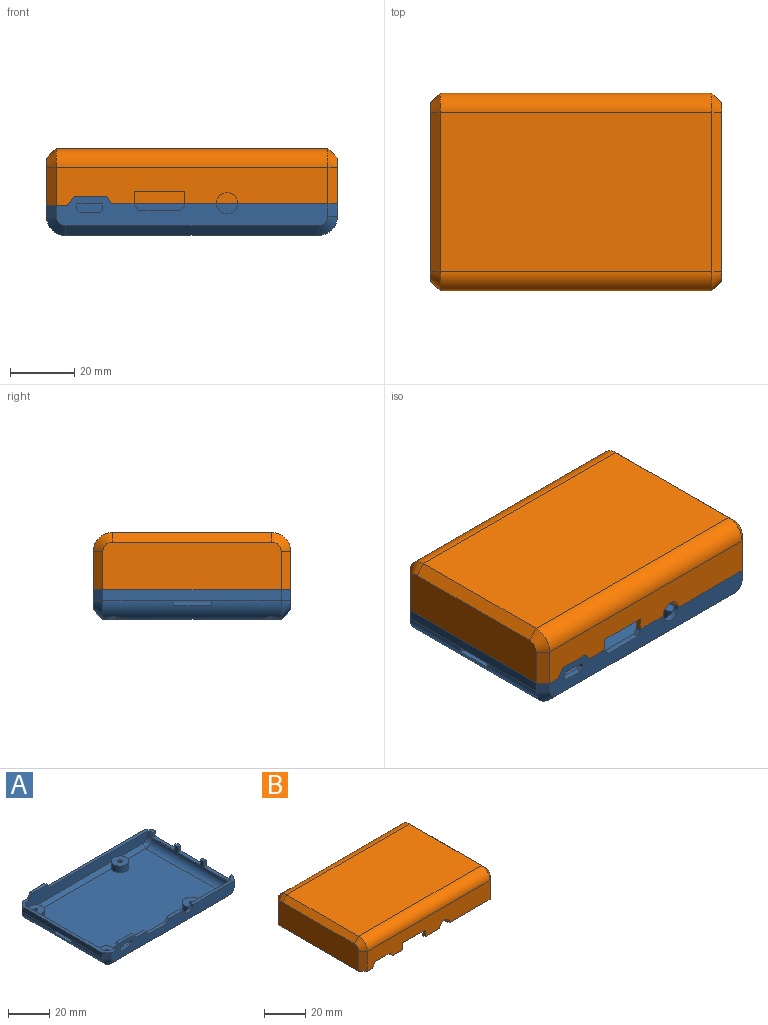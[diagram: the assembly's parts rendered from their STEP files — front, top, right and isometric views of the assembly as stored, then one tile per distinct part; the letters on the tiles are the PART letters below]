
ASSEMBLY  parts=2 mates=1
PART A: 98 faces, bbox 90.4x61.4x12.2 mm
  f0: plane 82.91x8.44mm, normal (0,1,0), area 457.5mm2, adj f8,f9,f10,f12,f14,f59,f60,f61
  f1: plane 84.4x9.18mm, normal (0,-1,0), area 527.3mm2, adj f41,f42,f43,f45,f47,f59,f60,f61
  f2: plane 53.91x3.8mm, normal (-1,0,0), area 48.1mm2, adj f6,f8,f11,f26,f27,f28,f29,f30
  f3: plane 78.4x53.91mm, normal (0,0,1), area 4076.9mm2, adj f6,f7,f10,f15,f18,f20,f22,f24
  f4: plane 53.91x3.18mm, normal (1,0,0), area 171.2mm2, adj f7,f14,f17,f72,f88
  f5: plane 82.91x8.44mm, normal (0,-1,0), area 525.6mm2, adj f11,f13,f15,f16,f17,f87,f88,f89
  f6: cylinder r=4.2mm len=53.91mm, axis (0,1,0), area 355.7mm2, adj f2,f3,f9,f13
  f7: cylinder r=4.2mm len=53.91mm, axis (0,-1,0), area 275.8mm2, adj f3,f4,f12,f16,f18,f20,f71,f73
  f8: plane 3.8x1.95mm, normal (-0.71,0.71,0), area 10.4mm2, adj f0,f2,f9,f85
  f9: cone r=1.73mm half-angle=45deg, axis (0,1,0), area 13.9mm2, adj f0,f6,f8,f10
  f10: plane 78.4x1.95mm, normal (0,0.71,0.71), area 195.8mm2, adj f0,f3,f9,f12,f18,f24
  f11: plane 3.8x1.95mm, normal (-0.71,-0.71,0), area 10.4mm2, adj f2,f5,f13,f87
  f12: cone r=1.73mm half-angle=45deg, axis (0,1,0), area 7.2mm2, adj f0,f7,f10,f14,f18
  f13: cone r=1.73mm half-angle=45deg, axis (0,-1,0), area 13.9mm2, adj f5,f6,f11,f15
  f14: plane 3.18x1.95mm, normal (0.71,0.71,0), area 8.7mm2, adj f0,f4,f12,f88
  f15: plane 78.4x1.95mm, normal (0,-0.71,0.71), area 195.8mm2, adj f3,f5,f13,f16,f20,f22
  f16: cone r=1.73mm half-angle=45deg, axis (0,-1,0), area 7.2mm2, adj f5,f7,f15,f17,f20
  f17: plane 3.18x1.95mm, normal (0.71,-0.71,0), area 8.7mm2, adj f4,f5,f16,f88
  f18: cylinder r=4.3mm len=8.6mm, axis (0,0,-1), area 76.6mm2, adj f3,f7,f10,f12,f19
  f19: plane 8.6x8.6mm, normal (0,0,1), area 54.9mm2, adj f18,f78
  f20: cylinder r=4.3mm len=8.6mm, axis (0,0,-1), area 76.6mm2, adj f3,f7,f15,f16,f21
  f21: plane 8.6x8.6mm, normal (0,0,1), area 54.9mm2, adj f20,f77
  f22: cylinder r=4.3mm len=8.6mm, axis (0,0,-1), area 95.3mm2, adj f3,f15,f23
  f23: plane 8.6x8.6mm, normal (0,0,1), area 54.9mm2, adj f22,f76
  f24: cylinder r=4.3mm len=8.6mm, axis (0,0,-1), area 95.3mm2, adj f3,f10,f25
  f25: plane 8.6x8.6mm, normal (0,0,1), area 54.9mm2, adj f24,f75
  f26: plane 3.3x1.8mm, normal (0,1,0), area 5.9mm2, adj f2,f27,f35,f97
  f27: plane 15x1.8mm, normal (0,0,1), area 27mm2, adj f2,f26,f28,f35
  f28: plane 3.3x1.8mm, normal (0,-1,0), area 5.9mm2, adj f2,f27,f35,f87
  f29: plane 3.3x1.8mm, normal (0,1,0), area 5.9mm2, adj f2,f30,f35,f96
  f30: plane 15x1.8mm, normal (0,0,1), area 27mm2, adj f2,f29,f31,f35
  f31: plane 3.3x1.8mm, normal (0,-1,0), area 5.9mm2, adj f2,f30,f35,f97
  f32: plane 3.3x1.8mm, normal (0,1,0), area 5.9mm2, adj f2,f33,f35,f85
  f33: plane 17.5x1.8mm, normal (0,0,1), area 31.5mm2, adj f2,f32,f34,f35
  f34: plane 3.3x1.8mm, normal (0,-1,0), area 5.9mm2, adj f2,f33,f35,f96
  f35: plane 55.4x3.8mm, normal (1,0,0), area 53.7mm2, adj f26,f27,f28,f29,f30,f31,f32,f33
  f36: plane 78.4x55.4mm, normal (0,0,-1), area 4256.1mm2, adj f39,f40,f43,f48,f79,f81,f83,f84
  f37: plane 55.4x3.18mm, normal (-1,0,0), area 175.9mm2, adj f40,f47,f50,f72,f88
  f38: plane 84.4x9.18mm, normal (0,1,0), area 595.4mm2, adj f44,f46,f48,f49,f50,f87,f88,f89
  f39: cylinder r=6mm len=55.4mm, axis (0,1,0), area 522.1mm2, adj f35,f36,f42,f46
  f40: cylinder r=6mm len=55.4mm, axis (0,-1,0), area 471.3mm2, adj f36,f37,f45,f49,f71,f73,f74,f80
  f41: plane 3.8x3mm, normal (0.71,-0.71,0), area 16.1mm2, adj f1,f35,f42,f85
  f42: cone r=3mm half-angle=45deg, axis (0,1,0), area 30mm2, adj f1,f39,f41,f43
  f43: plane 78.4x3mm, normal (0,-0.71,-0.71), area 332.6mm2, adj f1,f36,f42,f45
  f44: plane 3.8x3mm, normal (0.71,0.71,0), area 16.1mm2, adj f35,f38,f46,f87
  f45: cone r=3mm half-angle=45deg, axis (0,1,0), area 30mm2, adj f1,f40,f43,f47
  f46: cone r=3mm half-angle=45deg, axis (0,-1,0), area 30mm2, adj f38,f39,f44,f48
  f47: plane 3.18x3mm, normal (-0.71,-0.71,0), area 13.5mm2, adj f1,f37,f45,f88
  f48: plane 78.4x3mm, normal (0,0.71,-0.71), area 332.6mm2, adj f36,f38,f46,f49
  f49: cone r=3mm half-angle=45deg, axis (0,-1,0), area 30mm2, adj f38,f40,f48,f50
  f50: plane 3.18x3mm, normal (-0.71,0.71,0), area 13.5mm2, adj f37,f38,f49,f88
  f51: cylinder r=2.5mm len=5mm, axis (0,0,-1), area 50.6mm2, adj f52,f81,f82
  f52: plane 5x5mm, normal (0,0,-1), area 16.5mm2, adj f51,f78
  f53: cylinder r=2.5mm len=5mm, axis (0,0,-1), area 50.6mm2, adj f54,f79,f80
  f54: plane 5x5mm, normal (0,0,-1), area 16.5mm2, adj f53,f77
  f55: cylinder r=2.5mm len=5mm, axis (0,0,-1), area 53.4mm2, adj f56,f84
  f56: plane 5x5mm, normal (0,0,-1), area 16.5mm2, adj f55,f76
  f57: cylinder r=2.5mm len=5mm, axis (0,0,-1), area 53.4mm2, adj f58,f83
  f58: plane 5x5mm, normal (0,0,-1), area 16.5mm2, adj f57,f75
  f59: plane 1.81x1.8mm, normal (-1,0,0), area 3.3mm2, adj f0,f1,f60,f64
  f60: plane 8x1.8mm, normal (0,0,-1), area 14.4mm2, adj f0,f1,f59,f61
  f61: plane 1.84x1.8mm, normal (1,0,0), area 3.3mm2, adj f0,f1,f60,f62
  f62: plane 1.8x0.99mm, normal (0.71,0,0.71), area 2.5mm2, adj f0,f1,f61,f63
  f63: plane 6x1.8mm, normal (0,0,1), area 10.8mm2, adj f0,f1,f62,f64
  f64: plane 1.8x1.01mm, normal (-0.71,0,0.71), area 2.6mm2, adj f0,f1,f59,f63
  f65: plane 12.79x1.8mm, normal (0,0,1), area 23mm2, adj f0,f1,f66,f69
  f66: plane 1.8x1.45mm, normal (-0.75,0,0.66), area 3.5mm2, adj f0,f1,f65,f67
  f67: plane 1.8x0.67mm, normal (-1,0,0), area 1.2mm2, adj f0,f1,f66,f86
  f68: plane 1.8x0.38mm, normal (1,0,0), area 0.7mm2, adj f0,f1,f69,f94
  f69: plane 1.8x1.74mm, normal (0.75,0,0.66), area 4.2mm2, adj f0,f1,f65,f68
  f70: cylinder r=3.3mm len=6.59mm, axis (0,1,0), area 17.9mm2, adj f0,f1,f85,f86
  f71: plane 2.21x1.8mm, normal (0,-1,0), area 3.3mm2, adj f7,f40,f72,f74
  f72: plane 11.8x1.8mm, normal (0,0,-1), area 21.2mm2, adj f4,f37,f71,f73
  f73: plane 2.21x1.8mm, normal (0,1,0), area 3.3mm2, adj f7,f40,f72,f74
  f74: plane 11.8x1.93mm, normal (0,0,1), area 22.8mm2, adj f7,f40,f71,f73
  f75: cylinder r=1mm len=2mm, axis (0,0,-1), area 11.3mm2, adj f25,f58
  f76: cylinder r=1mm len=2mm, axis (0,0,-1), area 11.3mm2, adj f23,f56
  f77: cylinder r=1mm len=2mm, axis (0,0,-1), area 11.3mm2, adj f21,f54
  f78: cylinder r=1mm len=2mm, axis (0,0,-1), area 11.3mm2, adj f19,f52
  f79: torus R=3mm, axis (0,0,1), area 6.9mm2, adj f36,f53,f80
  f80: bspline ~6.01x3.73mm, area 7.7mm2, adj f40,f53,f79
  f81: torus R=3mm, axis (0,0,1), area 6.9mm2, adj f36,f51,f82
  f82: bspline ~6.01x3.73mm, area 7.7mm2, adj f40,f51,f81
  f83: torus R=3mm, axis (0,0,1), area 13.2mm2, adj f36,f57
  f84: torus R=3mm, axis (0,0,1), area 13.2mm2, adj f36,f55
  f85: plane 31.01x4.55mm, normal (0,0,1), area 58.2mm2, adj f0,f1,f2,f8,f32,f35,f41,f70
  f86: plane 10.01x1.8mm, normal (0,0,1), area 18mm2, adj f0,f1,f67,f70
  f87: plane 70.18x4.35mm, normal (0,0,1), area 128.3mm2, adj f2,f5,f11,f28,f35,f38,f44,f91
  f88: plane 61.4x6.44mm, normal (0,0,1), area 122mm2, adj f0,f1,f4,f5,f14,f17,f37,f38
  f89: plane 3.01x2.17mm, normal (-0.81,0,0.58), area 6.7mm2, adj f5,f38,f88,f90
  f90: plane 10.07x1.8mm, normal (0,0,1), area 18.1mm2, adj f5,f38,f89,f91
  f91: plane 2.39x1.8mm, normal (0.84,0,0.54), area 5.1mm2, adj f5,f38,f87,f90
  f92: plane 3.01x2.17mm, normal (-0.81,0,0.58), area 6.7mm2, adj f0,f1,f88,f93
  f93: plane 10.07x1.8mm, normal (0,0,1), area 18.1mm2, adj f0,f1,f92,f95
  f94: plane 6.98x1.8mm, normal (0,0,1), area 12.6mm2, adj f0,f1,f68,f95
  f95: plane 2.39x1.8mm, normal (0.84,0,0.54), area 5.1mm2, adj f0,f1,f93,f94
  f96: plane 2.4x1.8mm, normal (0,0,1), area 4.3mm2, adj f2,f29,f34,f35
  f97: plane 2.6x1.8mm, normal (0,0,1), area 4.7mm2, adj f2,f26,f31,f35
PART B: 81 faces, bbox 90.4x61.4x20 mm
  f0: cylinder r=4.2mm len=82.91mm, axis (-1,0,0), area 528.6mm2, adj f1,f2,f8,f47,f62,f71
  f1: cone r=1.73mm half-angle=45deg, axis (1,0,0), area 13.9mm2, adj f0,f6,f43,f44,f62
  f2: plane 82.91x49.4mm, normal (0,0,-1), area 4052.5mm2, adj f0,f5,f6,f7,f62,f67,f71,f77
  f3: plane 84.4x49.4mm, normal (0,0,1), area 4169.4mm2, adj f4,f14,f15,f16
  f4: cylinder r=6mm len=84.4mm, axis (-1,0,0), area 795.5mm2, adj f3,f17,f19,f46
  f5: plane 49.4x1.95mm, normal (-0.71,0,-0.71), area 135.9mm2, adj f2,f8,f10,f39
  f6: plane 49.45x1.99mm, normal (0.71,0,-0.71), area 135.9mm2, adj f1,f2,f9,f44,f62,f67
  f7: cylinder r=4.2mm len=82.91mm, axis (1,0,0), area 528.6mm2, adj f2,f9,f10,f42,f67,f77
  f8: cone r=1.73mm half-angle=45deg, axis (-1,0,0), area 13.9mm2, adj f0,f5,f25,f39
  f9: cone r=1.73mm half-angle=45deg, axis (1,0,0), area 13.9mm2, adj f6,f7,f40,f44,f67
  f10: cone r=1.73mm half-angle=45deg, axis (-1,0,0), area 13.8mm2, adj f5,f7,f11,f37,f39,f41,f45
  f11: plane 15x2.14mm, normal (0,0,-1), area 27.1mm2, adj f10,f32,f37,f38,f39
  f12: plane 15x1.8mm, normal (0,0,-1), area 27mm2, adj f32,f35,f36,f39
  f13: plane 17.5x1.8mm, normal (0,0,-1), area 31.5mm2, adj f32,f33,f34,f39
  f14: plane 49.4x3mm, normal (0.71,0,0.71), area 209.6mm2, adj f3,f17,f18,f32
  f15: plane 49.4x3mm, normal (-0.71,0,0.71), area 209.6mm2, adj f3,f19,f20,f31
  f16: cylinder r=6mm len=84.4mm, axis (1,0,0), area 795.5mm2, adj f3,f18,f20,f29
  f17: cone r=3mm half-angle=45deg, axis (-1,0,0), area 30mm2, adj f4,f14,f26,f32
  f18: cone r=3mm half-angle=45deg, axis (-1,0,0), area 30mm2, adj f14,f16,f27,f32
  f19: cone r=3mm half-angle=45deg, axis (1,0,0), area 30mm2, adj f4,f15,f30,f31
  f20: cone r=3mm half-angle=45deg, axis (1,0,0), area 30mm2, adj f15,f16,f28,f31
  f21: plane 15.6x1.8mm, normal (0,0,-1), area 28.1mm2, adj f23,f24,f46,f47
  f22: cylinder r=3.3mm len=6.6mm, axis (0,1,0), area 19.4mm2, adj f46,f47,f48,f49
  f23: plane 4x1.8mm, normal (-1,0,0), area 7.2mm2, adj f21,f46,f47,f49
  f24: plane 4x1.8mm, normal (1,0,0), area 7.2mm2, adj f21,f46,f47,f57
  f25: plane 11.2x1.95mm, normal (-0.71,0.71,0), area 30.8mm2, adj f8,f39,f47,f48
  f26: plane 11.2x3mm, normal (0.71,-0.71,0), area 47.5mm2, adj f17,f32,f46,f48
  f27: plane 11.2x3mm, normal (0.71,0.71,0), area 47.5mm2, adj f18,f29,f32,f50
  f28: plane 11.82x3mm, normal (-0.71,0.71,0), area 50.2mm2, adj f20,f29,f31,f51
  f29: plane 84.4x11.82mm, normal (0,1,0), area 919.9mm2, adj f16,f27,f28,f50,f51,f52,f53,f54
  f30: plane 11.82x3mm, normal (-0.71,-0.71,0), area 50.2mm2, adj f19,f31,f46,f51
  f31: plane 55.4x14.82mm, normal (-1,0,0), area 817.4mm2, adj f15,f19,f20,f28,f30,f51
  f32: plane 55.4x14.2mm, normal (1,0,0), area 182.1mm2, adj f11,f12,f13,f14,f17,f18,f26,f27
  f33: plane 11.7x1.8mm, normal (0,-1,0), area 21.1mm2, adj f13,f32,f39,f59
  f34: plane 11.7x1.8mm, normal (0,1,0), area 21.1mm2, adj f13,f32,f39,f48
  f35: plane 13.2x1.8mm, normal (0,-1,0), area 23.8mm2, adj f12,f32,f39,f60
  f36: plane 13.2x1.8mm, normal (0,1,0), area 23.8mm2, adj f12,f32,f39,f59
  f37: plane 13.23x2.17mm, normal (0,-1,0), area 23.8mm2, adj f10,f11,f32,f45,f50
  f38: plane 13.2x1.8mm, normal (0,1,0), area 23.8mm2, adj f11,f32,f39,f60
  f39: plane 52.69x13.46mm, normal (-1,0,0), area 115.1mm2, adj f5,f8,f10,f11,f12,f13,f25,f33
  f40: plane 11.82x1.95mm, normal (0.71,-0.71,0), area 32.5mm2, adj f9,f42,f44,f51
  f41: plane 11.2x1.95mm, normal (-0.71,-0.71,0), area 30.8mm2, adj f10,f42,f45,f50
  f42: plane 82.91x11.82mm, normal (0,-1,0), area 902.7mm2, adj f7,f40,f41,f50,f51,f52,f53,f54
  f43: plane 11.82x1.95mm, normal (0.71,0.71,0), area 32.5mm2, adj f1,f44,f47,f51
  f44: plane 53.91x14.08mm, normal (1,0,0), area 756.8mm2, adj f1,f6,f9,f40,f43,f51
  f45: plane 12.74x0.6mm, normal (-1,0,0), area 7.4mm2, adj f10,f37,f41,f50
  f46: plane 84.4x11.82mm, normal (0,-1,0), area 839mm2, adj f4,f21,f22,f23,f24,f26,f30,f48
  f47: plane 82.91x11.82mm, normal (0,1,0), area 821.8mm2, adj f0,f21,f22,f23,f24,f25,f43,f48
  f48: plane 31.01x4.55mm, normal (0,0,-1), area 58.2mm2, adj f22,f25,f26,f32,f34,f39,f46,f47
  f49: plane 10.01x1.8mm, normal (0,0,-1), area 18mm2, adj f22,f23,f46,f47
  f50: plane 70.18x4.35mm, normal (0,0,-1), area 128.3mm2, adj f27,f29,f32,f37,f41,f42,f45,f54
  f51: plane 61.4x6.44mm, normal (0,0,-1), area 122mm2, adj f28,f29,f30,f31,f40,f42,f43,f44
  f52: plane 3.01x2.17mm, normal (0.81,0,-0.58), area 6.7mm2, adj f29,f42,f51,f53
  f53: plane 10.07x1.8mm, normal (0,0,-1), area 18.1mm2, adj f29,f42,f52,f54
  f54: plane 2.39x1.8mm, normal (-0.84,0,-0.54), area 5.1mm2, adj f29,f42,f50,f53
  f55: plane 3.01x2.17mm, normal (0.81,0,-0.58), area 6.7mm2, adj f46,f47,f51,f56
  f56: plane 10.07x1.8mm, normal (0,0,-1), area 18.1mm2, adj f46,f47,f55,f58
  f57: plane 6.98x1.8mm, normal (0,0,-1), area 12.6mm2, adj f24,f46,f47,f58
  f58: plane 2.39x1.8mm, normal (-0.84,0,-0.54), area 5.1mm2, adj f46,f47,f56,f57
  f59: plane 2.4x1.8mm, normal (0,0,-1), area 4.3mm2, adj f32,f33,f36,f39
  f60: plane 2.6x1.8mm, normal (0,0,-1), area 4.7mm2, adj f32,f35,f38,f39
  f61: cylinder r=1mm len=18.2mm, axis (0,0,1), area 114.2mm2, adj f63,f64,f65
  f62: cylinder r=2.5mm len=18.2mm, axis (0,0,1), area 283.3mm2, adj f0,f1,f2,f6,f63
  f63: plane 5x5mm, normal (0,0,-1), area 16.5mm2, adj f61,f62
  f64: cylinder r=4.2mm len=1.96mm, axis (-1,0,0), area 1.2mm2, adj f61,f65
  f65: plane 2x1.2mm, normal (0,0,-1), area 2mm2, adj f61,f64
  f66: cylinder r=1mm len=18.2mm, axis (0,0,1), area 114.2mm2, adj f68,f69,f70
  f67: cylinder r=2.5mm len=18.2mm, axis (0,0,1), area 283.4mm2, adj f2,f6,f7,f9,f68
  f68: plane 5x5mm, normal (0,0,-1), area 16.5mm2, adj f66,f67
  f69: cylinder r=4.2mm len=1.96mm, axis (1,0,0), area 1.2mm2, adj f66,f70
  f70: plane 2x1.2mm, normal (0,0,-1), area 2mm2, adj f66,f69
  f71: cylinder r=2.5mm len=18.2mm, axis (0,0,1), area 283.4mm2, adj f0,f2,f73
  f72: cylinder r=1mm len=18.2mm, axis (0,0,1), area 114.2mm2, adj f73,f74,f75
  f73: plane 5x5mm, normal (0,0,-1), area 16.5mm2, adj f71,f72
  f74: cylinder r=4.2mm len=1.96mm, axis (-1,0,0), area 1.2mm2, adj f72,f75
  f75: plane 2x1.2mm, normal (0,0,-1), area 2mm2, adj f72,f74
  f76: cylinder r=1mm len=18.2mm, axis (0,0,1), area 114.2mm2, adj f78,f79,f80
  f77: cylinder r=2.5mm len=18.2mm, axis (0,0,1), area 283.4mm2, adj f2,f7,f78
  f78: plane 5x5mm, normal (0,0,-1), area 16.5mm2, adj f76,f77
  f79: cylinder r=4.2mm len=1.96mm, axis (1,0,0), area 1.2mm2, adj f76,f80
  f80: plane 2x1.2mm, normal (0,0,-1), area 2mm2, adj f76,f79
PLACE A at identity
PLACE B at identity
MATE fastened B.f61 <-> A.f18  axis (0,0,-1) through (-39,-24.5,0)mm
